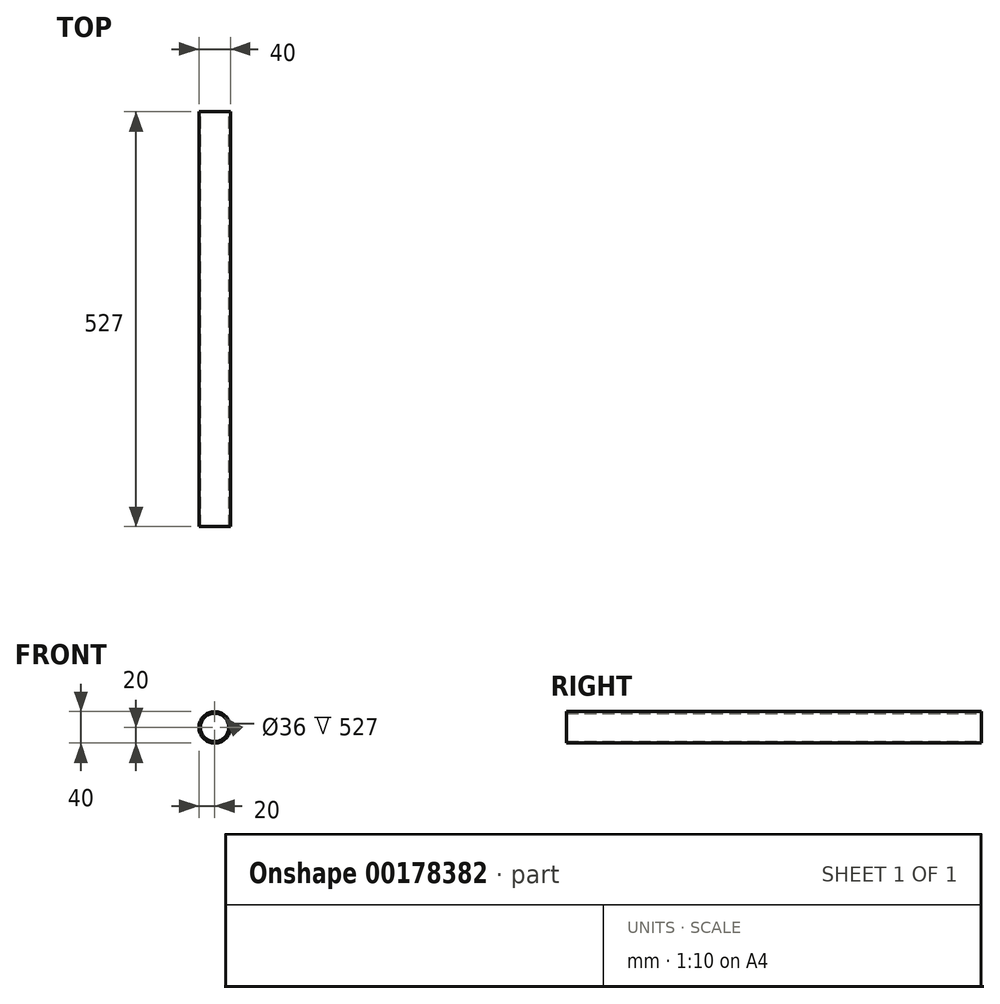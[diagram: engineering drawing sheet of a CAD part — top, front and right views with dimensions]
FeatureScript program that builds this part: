
annotation { "Feature Type Name" : "Feature", "Feature Type Description" : "" }
export const myFeature = defineFeature(function(context is Context, id is Id, definition is map)
    precondition{}
    {
        {
            var Q0;
            Q0=qCreatedBy(makeId("Front.planeOp"),FACE);
            var sketch = newSketch(context, id + "F0", { "sketchPlane" : qUnion([Q0])});
            skCircle(sketch, "E0", {"center": v(0, 0) * mm, "radius": 20 * mm});
            skCircle(sketch, "E1.0", {"center": v(0, 0) * mm, "radius": 18 * mm});
            skSolve(sketch);
        }
        {
            var Q0;
            Q0=makeQuery(id+"F0.imprint","IMPRINT",FACE,{"disambiguationData":[TD([[makeQuery(id+"F0.imprint","IMPRINT",EDGE,{"derivedFrom":sQuery(id+"F0.wireOp",EDGE,"E0")}),1.0]])]});
            extrude(context, id + "F1", {"entities" : qUnion([Q0]), "depth" : 527 * mm});
        }
    });
